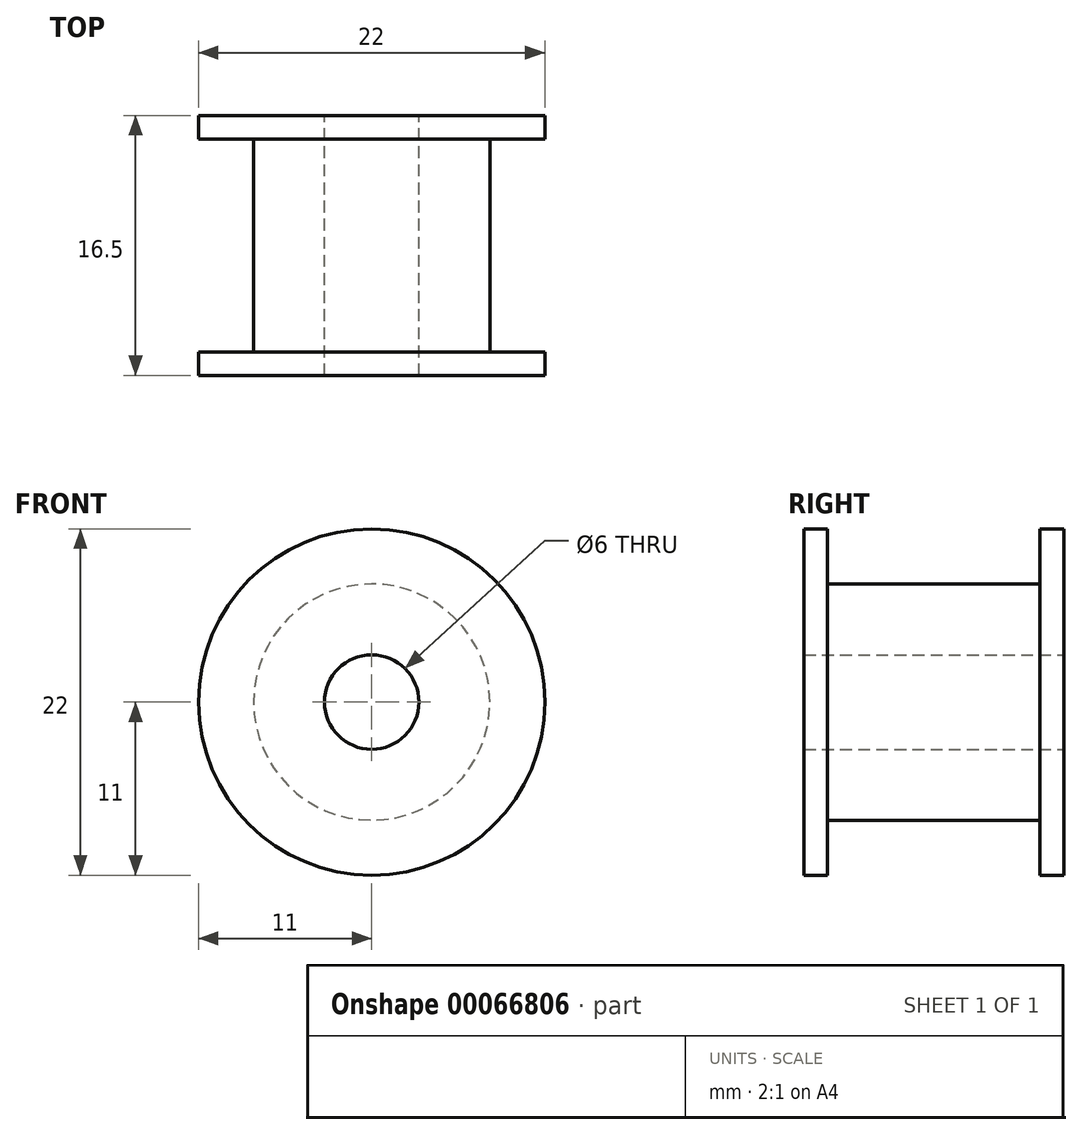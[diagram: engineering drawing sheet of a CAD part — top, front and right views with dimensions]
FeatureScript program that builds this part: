
annotation { "Feature Type Name" : "Feature", "Feature Type Description" : "" }
export const myFeature = defineFeature(function(context is Context, id is Id, definition is map)
    precondition{}
    {
        {
            var Q0;
            Q0=qCreatedBy(makeId("Front.planeOp"),FACE);
            var sketch = newSketch(context, id + "F0", { "sketchPlane" : qUnion([Q0])});
            skCircle(sketch, "E0", {"center": v(0, 0) * mm, "radius": 11 * mm});
            skCircle(sketch, "E1", {"center": v(0, 0) * mm, "radius": 7.5 * mm});
            skCircle(sketch, "E2", {"center": v(0, 0) * mm, "radius": 3 * mm});
            skSolve(sketch);
        }
        {
            var Q0;
            Q0=makeQuery(id+"F0.imprint","IMPRINT",FACE,{"disambiguationData":[TD([[makeQuery(id+"F0.imprint","IMPRINT",EDGE,{"derivedFrom":sQuery(id+"F0.wireOp",EDGE,"E1")}),1.0]])]});
            extrude(context, id + "F1", {"entities" : qUnion([Q0]), "depth" : 15 * mm});
        }
        {
            var Q0;
            Q0=makeQuery(id+"F0.imprint","IMPRINT",FACE,{"disambiguationData":[TD([[makeQuery(id+"F0.imprint","IMPRINT",EDGE,{"derivedFrom":sQuery(id+"F0.wireOp",EDGE,"E0")}),1.0]])]});
            var Q1;
            Q1=makeQuery(id+"F1.opExtrude","CAP_FACE",FACE,{"disambiguationData":[OSD([sQuery(id+"F0.wireOp",EDGE,"E1"),sQuery(id+"F0.wireOp",EDGE,"E2")])],"isStart":false});
            extrude(context, id + "F2", {"entities" : qUnion([Q0, Q1]), "operationType" : NewBodyOperationType.ADD, "depth" : 1.5 * mm});
        }
        {
            var Q0;
            Q0=makeQuery(id+"F2.opExtrude","CAP_FACE",FACE,{"disambiguationData":[OSD([sQuery(id+"F0.wireOp",EDGE,"E0"),sQuery(id+"F0.wireOp",EDGE,"E1")])],"isStart":false});
            extrude(context, id + "F3", {"entities" : qUnion([Q0]), "operationType" : NewBodyOperationType.ADD, "depth" : 15 * mm, "hasSecondDirection" : true, "secondDirectionOppositeDirection" : false, "secondDirectionDepth" : 13.5 * mm});
        }
    });
